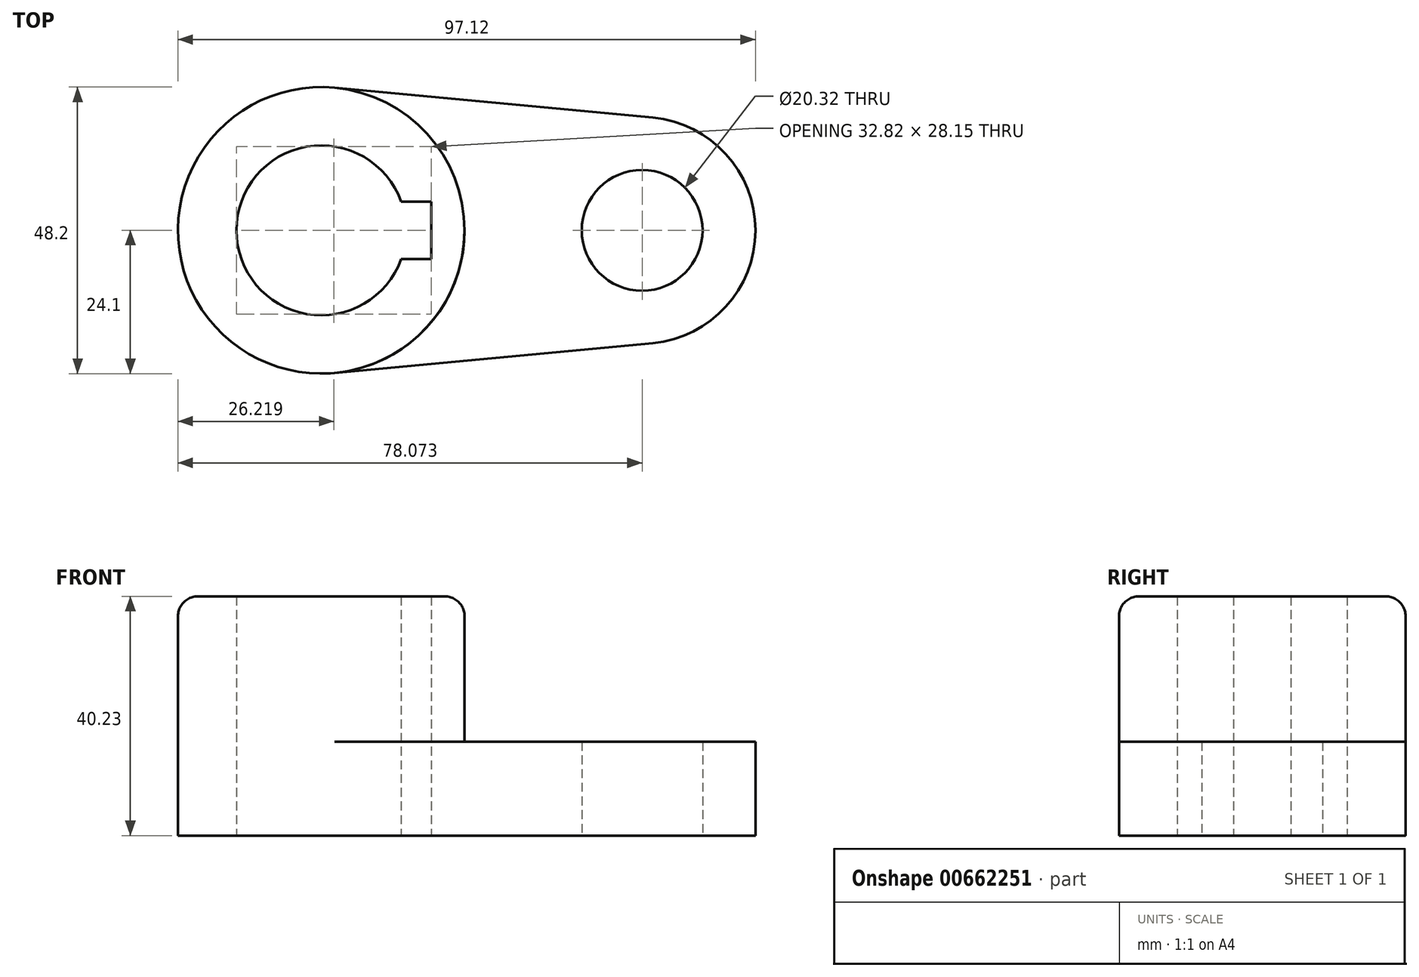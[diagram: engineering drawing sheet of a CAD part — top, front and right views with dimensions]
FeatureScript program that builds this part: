
annotation { "Feature Type Name" : "Feature", "Feature Type Description" : "" }
export const myFeature = defineFeature(function(context is Context, id is Id, definition is map)
    precondition{}
    {
        {
            var Q0;
            Q0=qCreatedBy(makeId("Top.planeOp"),FACE);
            var sketch = newSketch(context, id + "F0", { "sketchPlane" : qUnion([Q0])});
            skCircle(sketch, "E0", {"center": v(-29.63, 0) * mm, "radius": 24.1 * mm});
            skArc(sketch, "E1", {"start": v(26.13, -18.97) * mm, "mid": v(43.4, 0) * mm, "end": v(26.13, 18.97) * mm});
            skCircle(sketch, "E2", {"center": v(-29.63, 0) * mm, "radius": 14.29 * mm});
            skLineSegment(sketch, "E3", {"start": v(-16.18, 4.83) * mm, "end": v(-11.1, 4.83) * mm});
            skLineSegment(sketch, "E4", {"start": v(-16.18, -4.83) * mm, "end": v(-11.1, -4.83) * mm});
            skLineSegment(sketch, "E5", {"start": v(-11.1, 4.83) * mm, "end": v(-11.1, -4.83) * mm});
            skPoint(sketch, "E6.orphan", {"position": v(-6.02, 4.83) * mm});
            skPoint(sketch, "E7.orphan", {"position": v(-6.02, -4.83) * mm});
            skCircle(sketch, "E8", {"center": v(24.34, 0) * mm, "radius": 10.16 * mm});
            skLineSegment(sketch, "E9", {"start": v(-27.38, -24) * mm, "end": v(26.13, -18.97) * mm});
            skLineSegment(sketch, "E10", {"start": v(-27.38, 24) * mm, "end": v(26.13, 18.97) * mm});
            skSolve(sketch);
        }
        {
            var Q0;
            {var subQ0=sQuery(id+"F0.wireOp",EDGE,"E3");Q0=makeQuery(id+"F0.imprint","IMPRINT",FACE,{"disambiguationData":[TD([[makeQuery(id+"F0.imprint","IMPRINT",EDGE,{"derivedFrom":subQ0}),1.0]])]});}
            extrude(context, id + "F1", {"entities" : qUnion([Q0]), "depth" : 40.23 * mm, "offsetDistance" : 25.4 * mm});
        }
        {
            var Q0;
            {var subQ0=sQuery(id+"F0.wireOp",EDGE,"E9");Q0=makeQuery(id+"F0.imprint","IMPRINT",FACE,{"disambiguationData":[TD([[makeQuery(id+"F0.imprint","IMPRINT",EDGE,{"derivedFrom":subQ0}),1.0]])]});}
            var Q1;
            Q1=makeQuery(id+"F0.imprint","IMPRINT",FACE,{"disambiguationData":[TD([[makeQuery(id+"F0.imprint","IMPRINT",EDGE,{"derivedFrom":sQuery(id+"F0.wireOp",EDGE,"E8")}),-1.0]])]});
            extrude(context, id + "F2", {"entities" : qUnion([Q0, Q1]), "operationType" : NewBodyOperationType.ADD, "depth" : 15.77 * mm, "offsetDistance" : 25.4 * mm});
        }
        {
            var Q0;
            Q0=makeQuery(id+"F1.opExtrude","CAP_EDGE",EDGE,{"disambiguationData":[OSD([sQuery(id+"F0.wireOp",EDGE,"E0")])],"isStart":false});
            fillet(context, id + "F3", {"entities" : qUnion([Q0]), "radius" : 3.3 * mm, "tangentPropagation" : true, "allowEdgeOverflow" : false});
        }
    });
